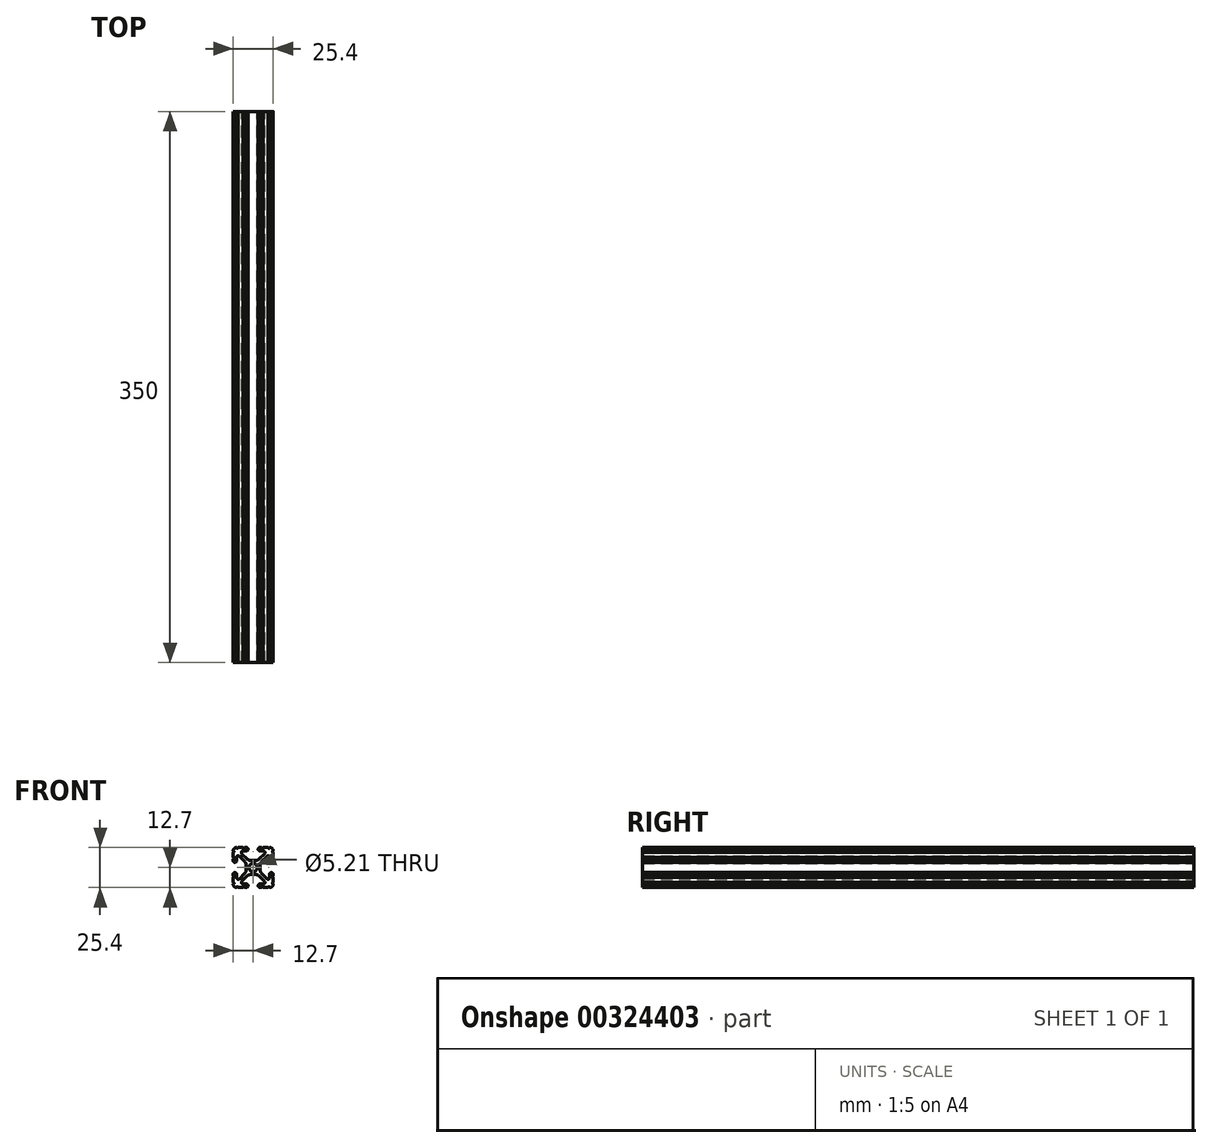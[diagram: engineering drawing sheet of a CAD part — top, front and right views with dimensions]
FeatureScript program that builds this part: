
annotation { "Feature Type Name" : "Feature", "Feature Type Description" : "" }
export const myFeature = defineFeature(function(context is Context, id is Id, definition is map)
    precondition{}
    {
        {
            var Q0;
            Q0=qCreatedBy(makeId("Front.planeOp"),FACE);
            var sketch = newSketch(context, id + "F0", { "sketchPlane" : qUnion([Q0])});
            skArc(sketch, "E0", {"start": v(-12.7, -10.57) * mm, "mid": v(-12.2, -10.06) * mm, "end": v(-12.7, -9.55) * mm});
            skArc(sketch, "E1", {"start": v(-12.7, -10.57) * mm, "mid": v(-12.08, -12.08) * mm, "end": v(-10.57, -12.7) * mm});
            skArc(sketch, "E2", {"start": v(-9.55, -12.7) * mm, "mid": v(-10.06, -12.2) * mm, "end": v(-10.57, -12.7) * mm});
            skLineSegment(sketch, "E3", {"start": v(-9.55, -12.7) * mm, "end": v(-6.33, -12.7) * mm});
            skArc(sketch, "E4", {"start": v(-5.32, -12.7) * mm, "mid": v(-5.83, -12.2) * mm, "end": v(-6.33, -12.7) * mm});
            skLineSegment(sketch, "E5", {"start": v(-5.32, -12.7) * mm, "end": v(-4.34, -12.7) * mm});
            skArc(sketch, "E6", {"start": v(-4.34, -12.7) * mm, "mid": v(-3.24, -11.6) * mm, "end": v(-4.34, -10.5) * mm});
            skLineSegment(sketch, "E7", {"start": v(-4.34, -10.5) * mm, "end": v(-6.47, -10.5) * mm});
            skArc(sketch, "E8", {"start": v(-7.2, -8.76) * mm, "mid": v(-7.41, -9.86) * mm, "end": v(-6.47, -10.5) * mm});
            skLineSegment(sketch, "E9", {"start": v(-7.2, -8.76) * mm, "end": v(-3.86, -5.43) * mm});
            skArc(sketch, "E10", {"start": v(-1.62, -4.5) * mm, "mid": v(-2.83, -4.74) * mm, "end": v(-3.86, -5.43) * mm});
            skLineSegment(sketch, "E11", {"start": v(-1.62, -4.5) * mm, "end": v(1.62, -4.5) * mm});
            skArc(sketch, "E12", {"start": v(3.86, -5.43) * mm, "mid": v(2.83, -4.74) * mm, "end": v(1.62, -4.5) * mm});
            skLineSegment(sketch, "E13", {"start": v(3.86, -5.43) * mm, "end": v(7.2, -8.76) * mm});
            skArc(sketch, "E14", {"start": v(6.47, -10.5) * mm, "mid": v(7.41, -9.86) * mm, "end": v(7.2, -8.76) * mm});
            skLineSegment(sketch, "E15", {"start": v(6.47, -10.5) * mm, "end": v(4.34, -10.5) * mm});
            skArc(sketch, "E16", {"start": v(4.34, -10.5) * mm, "mid": v(3.24, -11.6) * mm, "end": v(4.34, -12.7) * mm});
            skLineSegment(sketch, "E17", {"start": v(4.34, -12.7) * mm, "end": v(5.32, -12.7) * mm});
            skArc(sketch, "E18", {"start": v(6.33, -12.7) * mm, "mid": v(5.83, -12.2) * mm, "end": v(5.32, -12.7) * mm});
            skLineSegment(sketch, "E19", {"start": v(6.33, -12.7) * mm, "end": v(9.55, -12.7) * mm});
            skArc(sketch, "E20", {"start": v(10.57, -12.7) * mm, "mid": v(10.06, -12.2) * mm, "end": v(9.55, -12.7) * mm});
            skArc(sketch, "E21", {"start": v(10.57, -12.7) * mm, "mid": v(12.08, -12.08) * mm, "end": v(12.7, -10.57) * mm});
            skArc(sketch, "E22", {"start": v(12.7, -9.55) * mm, "mid": v(12.2, -10.06) * mm, "end": v(12.7, -10.57) * mm});
            skLineSegment(sketch, "E23", {"start": v(12.7, -9.55) * mm, "end": v(12.7, -6.33) * mm});
            skArc(sketch, "E24", {"start": v(12.7, -5.32) * mm, "mid": v(12.2, -5.83) * mm, "end": v(12.7, -6.33) * mm});
            skLineSegment(sketch, "E25", {"start": v(12.7, -5.32) * mm, "end": v(12.7, -4.34) * mm});
            skArc(sketch, "E26", {"start": v(12.7, -4.34) * mm, "mid": v(11.6, -3.24) * mm, "end": v(10.5, -4.34) * mm});
            skLineSegment(sketch, "E27", {"start": v(10.5, -4.34) * mm, "end": v(10.5, -6.47) * mm});
            skArc(sketch, "E28", {"start": v(8.76, -7.2) * mm, "mid": v(9.86, -7.41) * mm, "end": v(10.5, -6.47) * mm});
            skLineSegment(sketch, "E29", {"start": v(8.76, -7.2) * mm, "end": v(5.43, -3.86) * mm});
            skArc(sketch, "E30", {"start": v(4.5, -1.62) * mm, "mid": v(4.74, -2.83) * mm, "end": v(5.43, -3.86) * mm});
            skLineSegment(sketch, "E31", {"start": v(4.5, -1.62) * mm, "end": v(4.5, 1.62) * mm});
            skArc(sketch, "E32", {"start": v(5.43, 3.86) * mm, "mid": v(4.74, 2.83) * mm, "end": v(4.5, 1.62) * mm});
            skLineSegment(sketch, "E33", {"start": v(5.43, 3.86) * mm, "end": v(8.76, 7.2) * mm});
            skArc(sketch, "E34", {"start": v(10.5, 6.47) * mm, "mid": v(9.86, 7.41) * mm, "end": v(8.76, 7.2) * mm});
            skLineSegment(sketch, "E35", {"start": v(10.5, 6.47) * mm, "end": v(10.5, 4.34) * mm});
            skArc(sketch, "E36", {"start": v(10.5, 4.34) * mm, "mid": v(11.6, 3.24) * mm, "end": v(12.7, 4.34) * mm});
            skLineSegment(sketch, "E37", {"start": v(12.7, 4.34) * mm, "end": v(12.7, 5.32) * mm});
            skArc(sketch, "E38", {"start": v(12.7, 6.33) * mm, "mid": v(12.2, 5.83) * mm, "end": v(12.7, 5.32) * mm});
            skLineSegment(sketch, "E39", {"start": v(12.7, 6.33) * mm, "end": v(12.7, 9.55) * mm});
            skArc(sketch, "E40", {"start": v(12.7, 10.57) * mm, "mid": v(12.2, 10.06) * mm, "end": v(12.7, 9.55) * mm});
            skArc(sketch, "E41", {"start": v(12.7, 10.57) * mm, "mid": v(12.08, 12.08) * mm, "end": v(10.57, 12.7) * mm});
            skArc(sketch, "E42", {"start": v(9.55, 12.7) * mm, "mid": v(10.06, 12.2) * mm, "end": v(10.57, 12.7) * mm});
            skLineSegment(sketch, "E43", {"start": v(9.55, 12.7) * mm, "end": v(6.33, 12.7) * mm});
            skArc(sketch, "E44", {"start": v(5.32, 12.7) * mm, "mid": v(5.83, 12.2) * mm, "end": v(6.33, 12.7) * mm});
            skLineSegment(sketch, "E45", {"start": v(5.32, 12.7) * mm, "end": v(4.34, 12.7) * mm});
            skArc(sketch, "E46", {"start": v(4.34, 12.7) * mm, "mid": v(3.24, 11.6) * mm, "end": v(4.34, 10.5) * mm});
            skLineSegment(sketch, "E47", {"start": v(4.34, 10.5) * mm, "end": v(6.47, 10.5) * mm});
            skArc(sketch, "E48", {"start": v(7.2, 8.76) * mm, "mid": v(7.41, 9.86) * mm, "end": v(6.47, 10.5) * mm});
            skLineSegment(sketch, "E49", {"start": v(7.2, 8.76) * mm, "end": v(3.86, 5.43) * mm});
            skArc(sketch, "E50", {"start": v(1.62, 4.5) * mm, "mid": v(2.83, 4.74) * mm, "end": v(3.86, 5.43) * mm});
            skLineSegment(sketch, "E51", {"start": v(1.62, 4.5) * mm, "end": v(-1.62, 4.5) * mm});
            skArc(sketch, "E52", {"start": v(-3.86, 5.43) * mm, "mid": v(-2.83, 4.74) * mm, "end": v(-1.62, 4.5) * mm});
            skLineSegment(sketch, "E53", {"start": v(-3.86, 5.43) * mm, "end": v(-7.2, 8.76) * mm});
            skArc(sketch, "E54", {"start": v(-6.47, 10.5) * mm, "mid": v(-7.41, 9.86) * mm, "end": v(-7.2, 8.76) * mm});
            skLineSegment(sketch, "E55", {"start": v(-6.47, 10.5) * mm, "end": v(-4.34, 10.5) * mm});
            skArc(sketch, "E56", {"start": v(-4.34, 10.5) * mm, "mid": v(-3.24, 11.6) * mm, "end": v(-4.34, 12.7) * mm});
            skLineSegment(sketch, "E57", {"start": v(-4.34, 12.7) * mm, "end": v(-5.32, 12.7) * mm});
            skArc(sketch, "E58", {"start": v(-6.33, 12.7) * mm, "mid": v(-5.83, 12.2) * mm, "end": v(-5.32, 12.7) * mm});
            skLineSegment(sketch, "E59", {"start": v(-6.33, 12.7) * mm, "end": v(-9.55, 12.7) * mm});
            skArc(sketch, "E60", {"start": v(-10.57, 12.7) * mm, "mid": v(-10.06, 12.2) * mm, "end": v(-9.55, 12.7) * mm});
            skArc(sketch, "E61", {"start": v(-10.57, 12.7) * mm, "mid": v(-12.08, 12.08) * mm, "end": v(-12.7, 10.57) * mm});
            skArc(sketch, "E62", {"start": v(-12.7, 9.55) * mm, "mid": v(-12.2, 10.06) * mm, "end": v(-12.7, 10.57) * mm});
            skLineSegment(sketch, "E63", {"start": v(-12.7, 9.55) * mm, "end": v(-12.7, 6.33) * mm});
            skArc(sketch, "E64", {"start": v(-12.7, 5.32) * mm, "mid": v(-12.2, 5.83) * mm, "end": v(-12.7, 6.33) * mm});
            skLineSegment(sketch, "E65", {"start": v(-12.7, 5.32) * mm, "end": v(-12.7, 4.34) * mm});
            skArc(sketch, "E66", {"start": v(-12.7, 4.34) * mm, "mid": v(-11.6, 3.24) * mm, "end": v(-10.5, 4.34) * mm});
            skLineSegment(sketch, "E67", {"start": v(-10.5, 4.34) * mm, "end": v(-10.5, 6.47) * mm});
            skArc(sketch, "E68", {"start": v(-8.76, 7.2) * mm, "mid": v(-9.86, 7.41) * mm, "end": v(-10.5, 6.47) * mm});
            skLineSegment(sketch, "E69", {"start": v(-8.76, 7.2) * mm, "end": v(-5.43, 3.86) * mm});
            skArc(sketch, "E70", {"start": v(-4.5, 1.62) * mm, "mid": v(-4.74, 2.83) * mm, "end": v(-5.43, 3.86) * mm});
            skLineSegment(sketch, "E71", {"start": v(-4.5, 1.62) * mm, "end": v(-4.5, -1.62) * mm});
            skArc(sketch, "E72", {"start": v(-5.43, -3.86) * mm, "mid": v(-4.74, -2.83) * mm, "end": v(-4.5, -1.62) * mm});
            skLineSegment(sketch, "E73", {"start": v(-5.43, -3.86) * mm, "end": v(-8.76, -7.2) * mm});
            skArc(sketch, "E74", {"start": v(-10.5, -6.47) * mm, "mid": v(-9.86, -7.41) * mm, "end": v(-8.76, -7.2) * mm});
            skLineSegment(sketch, "E75", {"start": v(-10.5, -6.47) * mm, "end": v(-10.5, -4.34) * mm});
            skArc(sketch, "E76", {"start": v(-10.5, -4.34) * mm, "mid": v(-11.6, -3.24) * mm, "end": v(-12.7, -4.34) * mm});
            skLineSegment(sketch, "E77", {"start": v(-12.7, -4.34) * mm, "end": v(-12.7, -5.32) * mm});
            skArc(sketch, "E78", {"start": v(-12.7, -6.33) * mm, "mid": v(-12.2, -5.83) * mm, "end": v(-12.7, -5.32) * mm});
            skLineSegment(sketch, "E79", {"start": v(-12.7, -6.33) * mm, "end": v(-12.7, -9.55) * mm});
            skArc(sketch, "E80", {"start": v(2.6, 0) * mm, "mid": v(0, 2.6) * mm, "end": v(-2.6, 0) * mm});
            skArc(sketch, "E81", {"start": v(-2.6, 0) * mm, "mid": v(0, -2.6) * mm, "end": v(2.6, 0) * mm});
            skSolve(sketch);
        }
        {
            var Q0;
            Q0=makeQuery(id+"F0.imprint","IMPRINT",FACE,{"disambiguationData":[TD([[makeQuery(id+"F0.imprint","IMPRINT",EDGE,{"derivedFrom":sQuery(id+"F0.wireOp",EDGE,"E0")}),-1.0]])]});
            extrude(context, id + "F1", {"entities" : qUnion([Q0]), "depth" : 375 * mm});
        }
        {
            var Q0;
            Q0=makeQuery(id+"F1.opExtrude","CAP_FACE",FACE,{"disambiguationData":[OSD([sQuery(id+"F0.wireOp",EDGE,"E0"),sQuery(id+"F0.wireOp",EDGE,"E1"),sQuery(id+"F0.wireOp",EDGE,"E2"),sQuery(id+"F0.wireOp",EDGE,"E3"),sQuery(id+"F0.wireOp",EDGE,"E4"),sQuery(id+"F0.wireOp",EDGE,"E5"),sQuery(id+"F0.wireOp",EDGE,"E6"),sQuery(id+"F0.wireOp",EDGE,"E7"),sQuery(id+"F0.wireOp",EDGE,"E8"),sQuery(id+"F0.wireOp",EDGE,"E9"),sQuery(id+"F0.wireOp",EDGE,"E10"),sQuery(id+"F0.wireOp",EDGE,"E11"),sQuery(id+"F0.wireOp",EDGE,"E12"),sQuery(id+"F0.wireOp",EDGE,"E13"),sQuery(id+"F0.wireOp",EDGE,"E14"),sQuery(id+"F0.wireOp",EDGE,"E15"),sQuery(id+"F0.wireOp",EDGE,"E16"),sQuery(id+"F0.wireOp",EDGE,"E17"),sQuery(id+"F0.wireOp",EDGE,"E18"),sQuery(id+"F0.wireOp",EDGE,"E19"),sQuery(id+"F0.wireOp",EDGE,"E20"),sQuery(id+"F0.wireOp",EDGE,"E21"),sQuery(id+"F0.wireOp",EDGE,"E22"),sQuery(id+"F0.wireOp",EDGE,"E23"),sQuery(id+"F0.wireOp",EDGE,"E24"),sQuery(id+"F0.wireOp",EDGE,"E25"),sQuery(id+"F0.wireOp",EDGE,"E26"),sQuery(id+"F0.wireOp",EDGE,"E27"),sQuery(id+"F0.wireOp",EDGE,"E28"),sQuery(id+"F0.wireOp",EDGE,"E29"),sQuery(id+"F0.wireOp",EDGE,"E30"),sQuery(id+"F0.wireOp",EDGE,"E31"),sQuery(id+"F0.wireOp",EDGE,"E32"),sQuery(id+"F0.wireOp",EDGE,"E33"),sQuery(id+"F0.wireOp",EDGE,"E34"),sQuery(id+"F0.wireOp",EDGE,"E35"),sQuery(id+"F0.wireOp",EDGE,"E36"),sQuery(id+"F0.wireOp",EDGE,"E37"),sQuery(id+"F0.wireOp",EDGE,"E38"),sQuery(id+"F0.wireOp",EDGE,"E39"),sQuery(id+"F0.wireOp",EDGE,"E40"),sQuery(id+"F0.wireOp",EDGE,"E41"),sQuery(id+"F0.wireOp",EDGE,"E42"),sQuery(id+"F0.wireOp",EDGE,"E43"),sQuery(id+"F0.wireOp",EDGE,"E44"),sQuery(id+"F0.wireOp",EDGE,"E45"),sQuery(id+"F0.wireOp",EDGE,"E46"),sQuery(id+"F0.wireOp",EDGE,"E47"),sQuery(id+"F0.wireOp",EDGE,"E48"),sQuery(id+"F0.wireOp",EDGE,"E49"),sQuery(id+"F0.wireOp",EDGE,"E50"),sQuery(id+"F0.wireOp",EDGE,"E51"),sQuery(id+"F0.wireOp",EDGE,"E52"),sQuery(id+"F0.wireOp",EDGE,"E53"),sQuery(id+"F0.wireOp",EDGE,"E54"),sQuery(id+"F0.wireOp",EDGE,"E55"),sQuery(id+"F0.wireOp",EDGE,"E56"),sQuery(id+"F0.wireOp",EDGE,"E57"),sQuery(id+"F0.wireOp",EDGE,"E58"),sQuery(id+"F0.wireOp",EDGE,"E59"),sQuery(id+"F0.wireOp",EDGE,"E60"),sQuery(id+"F0.wireOp",EDGE,"E61"),sQuery(id+"F0.wireOp",EDGE,"E62"),sQuery(id+"F0.wireOp",EDGE,"E63"),sQuery(id+"F0.wireOp",EDGE,"E64"),sQuery(id+"F0.wireOp",EDGE,"E65"),sQuery(id+"F0.wireOp",EDGE,"E66"),sQuery(id+"F0.wireOp",EDGE,"E67"),sQuery(id+"F0.wireOp",EDGE,"E68"),sQuery(id+"F0.wireOp",EDGE,"E69"),sQuery(id+"F0.wireOp",EDGE,"E70"),sQuery(id+"F0.wireOp",EDGE,"E71"),sQuery(id+"F0.wireOp",EDGE,"E72"),sQuery(id+"F0.wireOp",EDGE,"E73"),sQuery(id+"F0.wireOp",EDGE,"E74"),sQuery(id+"F0.wireOp",EDGE,"E75"),sQuery(id+"F0.wireOp",EDGE,"E76"),sQuery(id+"F0.wireOp",EDGE,"E77"),sQuery(id+"F0.wireOp",EDGE,"E78"),sQuery(id+"F0.wireOp",EDGE,"E79"),sQuery(id+"F0.wireOp",EDGE,"E80"),sQuery(id+"F0.wireOp",EDGE,"E81")])],"isStart":false});
            extrude(context, id + "F2", {"entities" : qUnion([Q0]), "operationType" : NewBodyOperationType.REMOVE, "oppositeDirection" : true, "depth" : 25 * mm});
        }
    });
